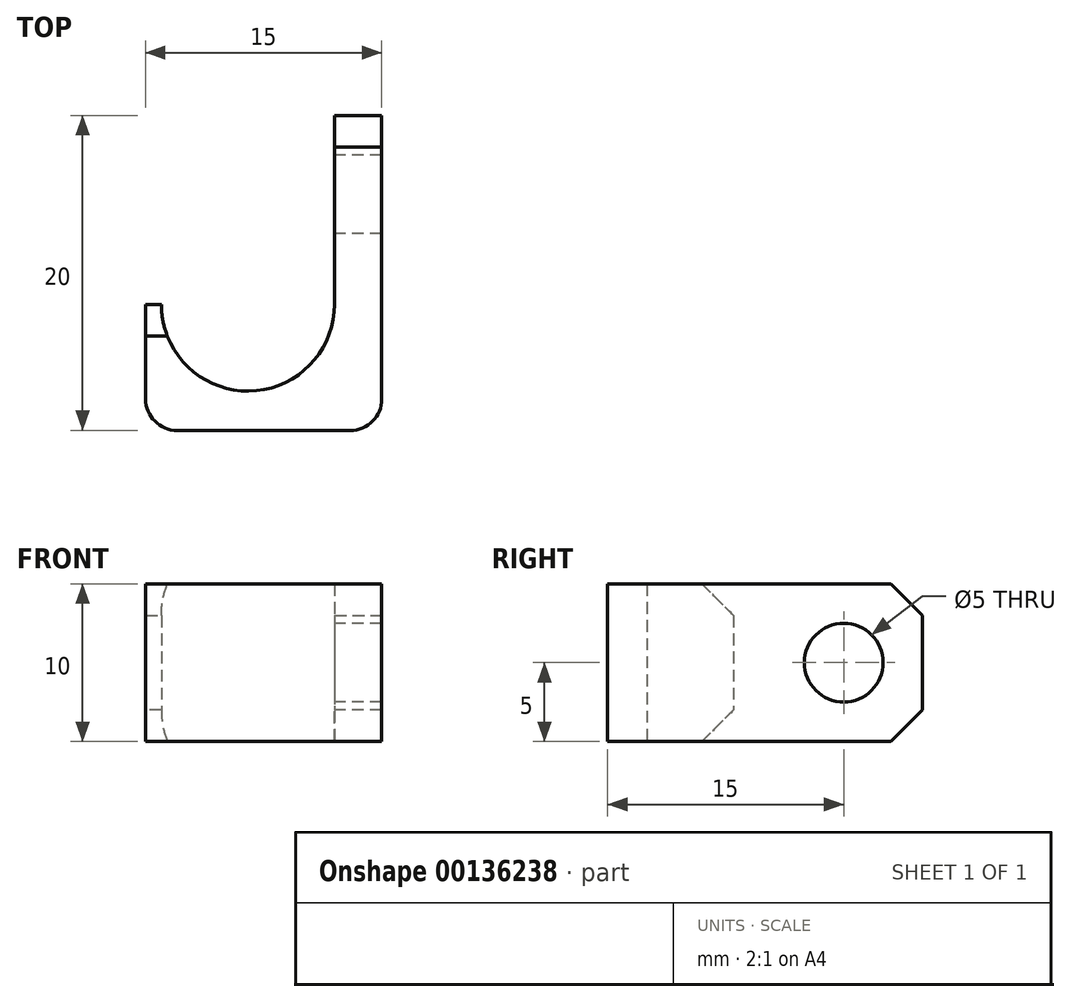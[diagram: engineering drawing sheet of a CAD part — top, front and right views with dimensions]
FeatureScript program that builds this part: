
annotation { "Feature Type Name" : "Feature", "Feature Type Description" : "" }
export const myFeature = defineFeature(function(context is Context, id is Id, definition is map)
    precondition{}
    {
        {
            var Q0;
            Q0=qCreatedBy(makeId("Top.planeOp"),FACE);
            var sketch = newSketch(context, id + "F0", { "sketchPlane" : qUnion([Q0])});
            skLineSegment(sketch, "E0", {"start": v(0, 2) * mm, "end": v(0, 20) * mm});
            skLineSegment(sketch, "E1", {"start": v(0, 20) * mm, "end": v(-3, 20) * mm});
            skLineSegment(sketch, "E2", {"start": v(-3, 20) * mm, "end": v(-3, 8) * mm});
            skLineSegment(sketch, "E3", {"start": v(-14, 8) * mm, "end": v(-15, 8) * mm});
            skLineSegment(sketch, "E4", {"start": v(-15, 8) * mm, "end": v(-15, 2) * mm});
            skLineSegment(sketch, "E5", {"start": v(-13, 0) * mm, "end": v(-2, 0) * mm});
            skArc(sketch, "E6", {"start": v(-14, 8) * mm, "mid": v(-8.5, 2.5) * mm, "end": v(-3, 8) * mm});
            skPoint(sketch, "E7.visualSharp", {"position": v(0, 0) * mm});
            skArc(sketch, "E7.filletArc", {"start": v(-2, 0) * mm, "mid": v(-0.59, 0.59) * mm, "end": v(0, 2) * mm});
            skPoint(sketch, "E8.visualSharp", {"position": v(-15, 0) * mm});
            skArc(sketch, "E8.filletArc", {"start": v(-15, 2) * mm, "mid": v(-14.41, 0.59) * mm, "end": v(-13, 0) * mm});
            skSolve(sketch);
        }
        {
            var Q0;
            Q0=makeQuery(id+"F0.imprint","IMPRINT",FACE,{"disambiguationData":[TD([[makeQuery(id+"F0.imprint","IMPRINT",EDGE,{"derivedFrom":sQuery(id+"F0.wireOp",EDGE,"E0")}),1.0]])]});
            extrude(context, id + "F1", {"entities" : qUnion([Q0]), "depth" : 10 * mm});
        }
        {
            var Q0;
            Q0=makeQuery(id+"F1.opExtrude","CAP_EDGE",EDGE,{"disambiguationData":[OSD([sQuery(id+"F0.wireOp",EDGE,"E1")])],"isStart":false});
            var Q1;
            Q1=makeQuery(id+"F1.opExtrude","CAP_EDGE",EDGE,{"disambiguationData":[OSD([sQuery(id+"F0.wireOp",EDGE,"E1")])],"isStart":true});
            var Q2;
            Q2=makeQuery(id+"F1.opExtrude","CAP_EDGE",EDGE,{"disambiguationData":[OSD([sQuery(id+"F0.wireOp",EDGE,"E3")])],"isStart":false});
            var Q3;
            Q3=makeQuery(id+"F1.opExtrude","CAP_EDGE",EDGE,{"disambiguationData":[OSD([sQuery(id+"F0.wireOp",EDGE,"E3")])],"isStart":true});
            chamfer(context, id + "F2", {"entities" : qUnion([Q0, Q1, Q2, Q3]), "width" : 2 * mm, "tangentPropagation" : true});
        }
        {
            var Q0;
            Q0=makeQuery(id+"F1.opExtrude","SWEPT_FACE",FACE,{"disambiguationData":[OSD([sQuery(id+"F0.wireOp",EDGE,"E2")])]});
            var sketch = newSketch(context, id + "F3", { "sketchPlane" : qUnion([Q0])});
            skCircle(sketch, "E9", {"center": v(-15, 5) * mm, "radius": 2.5 * mm});
            skSolve(sketch);
        }
        {
            var Q0;
            Q0=makeQuery(id+"F3.imprint","IMPRINT",FACE,{"disambiguationData":[TD([[makeQuery(id+"F3.imprint","IMPRINT",EDGE,{"derivedFrom":sQuery(id+"F3.wireOp",EDGE,"E9")}),1.0]])]});
            extrude(context, id + "F4", {"entities" : qUnion([Q0]), "operationType" : NewBodyOperationType.REMOVE, "oppositeDirection" : true, "depth" : 25 * mm});
        }
    });
